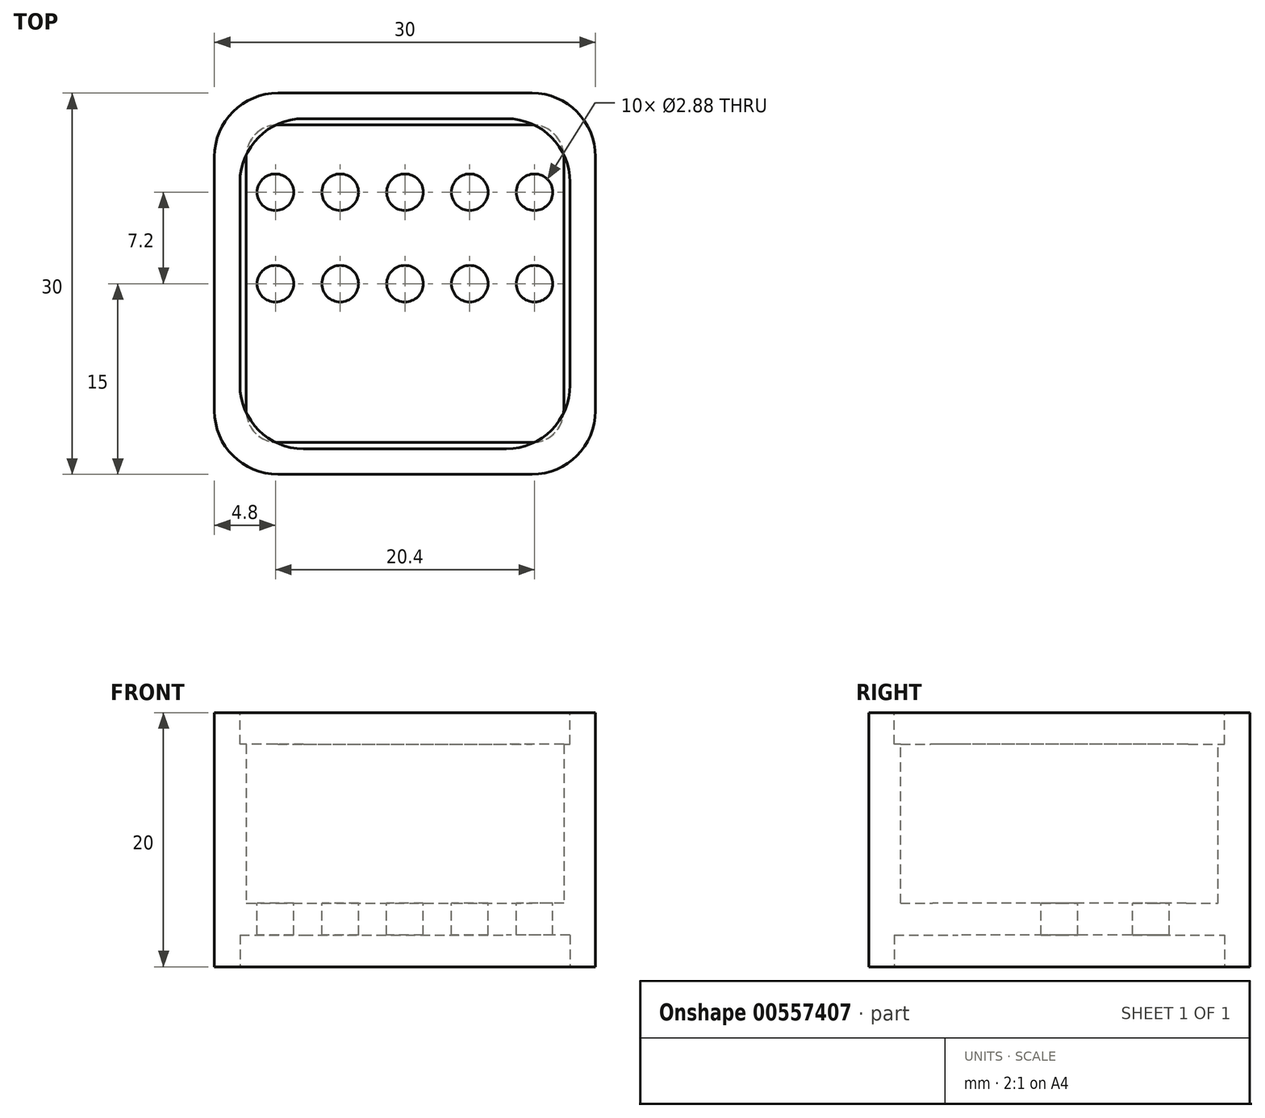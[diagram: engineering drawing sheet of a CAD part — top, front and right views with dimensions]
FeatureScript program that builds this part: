
annotation { "Feature Type Name" : "Feature", "Feature Type Description" : "" }
export const myFeature = defineFeature(function(context is Context, id is Id, definition is map)
    precondition{}
    {
        {
            var Q0;
            Q0=qCreatedBy(makeId("Top.planeOp"),FACE);
            var sketch = newSketch(context, id + "F0", { "sketchPlane" : qUnion([Q0])});
            skLineSegment(sketch, "E0.bottom", {"start": v(-15, 15) * mm, "end": v(15, 15) * mm});
            skLineSegment(sketch, "E0.top", {"start": v(-15, -15) * mm, "end": v(15, -15) * mm});
            skLineSegment(sketch, "E0.left", {"start": v(-15, 15) * mm, "end": v(-15, -15) * mm});
            skLineSegment(sketch, "E0.right", {"start": v(15, 15) * mm, "end": v(15, -15) * mm});
            skLineSegment(sketch, "E1.0", {"start": v(-13, 13) * mm, "end": v(13, 13) * mm, "construction": true});
            skLineSegment(sketch, "E1.1", {"start": v(-13, 13) * mm, "end": v(-13, -13) * mm, "construction": true});
            skLineSegment(sketch, "E1.2", {"start": v(-13, -13) * mm, "end": v(13, -13) * mm, "construction": true});
            skLineSegment(sketch, "E1.3", {"start": v(13, 13) * mm, "end": v(13, -13) * mm, "construction": true});
            skSolve(sketch);
        }
        {
            var Q0;
            Q0 = qSketchRegion(id + "F0", true);
            extrude(context, id + "F1", {"entities" : qUnion([Q0]), "depth" : 20 * mm, "offsetDistance" : 25 * mm});
        }
        {
            var Q0;
            Q0=makeQuery(id+"F0.imprint","IMPRINT",FACE,{"disambiguationData":[TD([[makeQuery(id+"F0.imprint","IMPRINT",EDGE,{"derivedFrom":sQuery(id+"F0.wireOp",EDGE,"E0.bottom")}),-1.0]])]});
            var sketch = newSketch(context, id + "F2", { "sketchPlane" : qUnion([Q0])});
            skLineSegment(sketch, "E2.0", {"start": v(-13, -13) * mm, "end": v(13, -13) * mm});
            skLineSegment(sketch, "E3.0", {"start": v(13, 13) * mm, "end": v(13, -13) * mm});
            skLineSegment(sketch, "E3.1", {"start": v(-13, 13) * mm, "end": v(13, 13) * mm});
            skLineSegment(sketch, "E3.2", {"start": v(-13, 13) * mm, "end": v(-13, -13) * mm});
            skSolve(sketch);
        }
        {
            var Q0;
            Q0 = qSketchRegion(id + "F2", true);
            extrude(context, id + "F3", {"entities" : qUnion([Q0]), "operationType" : NewBodyOperationType.REMOVE, "depth" : 2.5 * mm, "offsetDistance" : 25 * mm});
        }
        {
            var Q0;
            Q0=makeQuery(id+"F1.opExtrude","CAP_FACE",FACE,{"disambiguationData":[OSD([sQuery(id+"F0.wireOp",EDGE,"E0.bottom"),sQuery(id+"F0.wireOp",EDGE,"E0.top"),sQuery(id+"F0.wireOp",EDGE,"E0.left"),sQuery(id+"F0.wireOp",EDGE,"E0.right")])],"isStart":false});
            var sketch = newSketch(context, id + "F4", { "sketchPlane" : qUnion([Q0])});
            skLineSegment(sketch, "E4.0", {"start": v(-13, 13) * mm, "end": v(-13, -13) * mm});
            skLineSegment(sketch, "E4.1", {"start": v(-13, -13) * mm, "end": v(13, -13) * mm});
            skLineSegment(sketch, "E4.2", {"start": v(13, 13) * mm, "end": v(13, -13) * mm});
            skLineSegment(sketch, "E4.3", {"start": v(-13, 13) * mm, "end": v(13, 13) * mm});
            skSolve(sketch);
        }
        {
            var Q0;
            Q0 = qSketchRegion(id + "F4", true);
            extrude(context, id + "F5", {"entities" : qUnion([Q0]), "operationType" : NewBodyOperationType.REMOVE, "oppositeDirection" : true, "depth" : 2.5 * mm, "offsetDistance" : 25 * mm});
        }
        {
            var Q0;
            Q0=makeQuery(id+"F1.opExtrude","SWEPT_EDGE",EDGE,{"disambiguationData":[OSD([sQuery(id+"F0.wireOp",EDGE,"E0.top"),sQuery(id+"F0.wireOp",EDGE,"E0.left")])]});
            var Q1;
            Q1=makeQuery(id+"F5.boolean.opBoolean","COPY",EDGE,{"derivedFrom":makeQuery(id+"F5.opExtrude","SWEPT_EDGE",EDGE,{"disambiguationData":[OSD([sQuery(id+"F4.wireOp",EDGE,"E4.0"),sQuery(id+"F4.wireOp",EDGE,"E4.1")])]})});
            var Q2;
            Q2=makeQuery(id+"F5.boolean.opBoolean","COPY",EDGE,{"derivedFrom":makeQuery(id+"F5.opExtrude","SWEPT_EDGE",EDGE,{"disambiguationData":[OSD([sQuery(id+"F4.wireOp",EDGE,"E4.0"),sQuery(id+"F4.wireOp",EDGE,"E4.3")])]})});
            var Q3;
            Q3=makeQuery(id+"F5.boolean.opBoolean","COPY",EDGE,{"derivedFrom":makeQuery(id+"F5.opExtrude","SWEPT_EDGE",EDGE,{"disambiguationData":[OSD([sQuery(id+"F4.wireOp",EDGE,"E4.1"),sQuery(id+"F4.wireOp",EDGE,"E4.2")])]})});
            var Q4;
            Q4=makeQuery(id+"F1.opExtrude","SWEPT_EDGE",EDGE,{"disambiguationData":[OSD([sQuery(id+"F0.wireOp",EDGE,"E0.top"),sQuery(id+"F0.wireOp",EDGE,"E0.right")])]});
            var Q5;
            Q5=makeQuery(id+"F1.opExtrude","SWEPT_EDGE",EDGE,{"disambiguationData":[OSD([sQuery(id+"F0.wireOp",EDGE,"E0.bottom"),sQuery(id+"F0.wireOp",EDGE,"E0.right")])]});
            var Q6;
            Q6=makeQuery(id+"F1.opExtrude","SWEPT_EDGE",EDGE,{"disambiguationData":[OSD([sQuery(id+"F0.wireOp",EDGE,"E0.bottom"),sQuery(id+"F0.wireOp",EDGE,"E0.left")])]});
            var Q7;
            Q7=makeQuery(id+"F5.boolean.opBoolean","COPY",EDGE,{"derivedFrom":makeQuery(id+"F5.opExtrude","SWEPT_EDGE",EDGE,{"disambiguationData":[OSD([sQuery(id+"F4.wireOp",EDGE,"E4.2"),sQuery(id+"F4.wireOp",EDGE,"E4.3")])]})});
            var Q8;
            Q8=makeQuery(id+"F3.boolean.opBoolean","COPY",EDGE,{"derivedFrom":makeQuery(id+"F3.opExtrude","SWEPT_EDGE",EDGE,{"disambiguationData":[OSD([sQuery(id+"F2.wireOp",EDGE,"E3.1"),sQuery(id+"F2.wireOp",EDGE,"E3.2")])]})});
            var Q9;
            Q9=makeQuery(id+"F3.boolean.opBoolean","COPY",EDGE,{"derivedFrom":makeQuery(id+"F3.opExtrude","SWEPT_EDGE",EDGE,{"disambiguationData":[OSD([sQuery(id+"F2.wireOp",EDGE,"E2.0"),sQuery(id+"F2.wireOp",EDGE,"E3.0")])]})});
            var Q10;
            Q10=makeQuery(id+"F3.boolean.opBoolean","COPY",EDGE,{"derivedFrom":makeQuery(id+"F3.opExtrude","SWEPT_EDGE",EDGE,{"disambiguationData":[OSD([sQuery(id+"F2.wireOp",EDGE,"E2.0"),sQuery(id+"F2.wireOp",EDGE,"E3.2")])]})});
            var Q11;
            Q11=makeQuery(id+"F3.boolean.opBoolean","COPY",EDGE,{"derivedFrom":makeQuery(id+"F3.opExtrude","SWEPT_EDGE",EDGE,{"disambiguationData":[OSD([sQuery(id+"F2.wireOp",EDGE,"E3.0"),sQuery(id+"F2.wireOp",EDGE,"E3.1")])]})});
            fillet(context, id + "F6", {"entities" : qUnion([Q0, Q1, Q2, Q3, Q4, Q5, Q6, Q7, Q8, Q9, Q10, Q11]), "radius" : 5 * mm, "tangentPropagation" : true, "allowEdgeOverflow" : false});
        }
        {
            var Q0;
            Q0=makeQuery(id+"F5.boolean.opBoolean","COPY",FACE,{"derivedFrom":makeQuery(id+"F5.opExtrude","CAP_FACE",FACE,{"disambiguationData":[OSD([sQuery(id+"F4.wireOp",EDGE,"E4.0"),sQuery(id+"F4.wireOp",EDGE,"E4.1"),sQuery(id+"F4.wireOp",EDGE,"E4.2"),sQuery(id+"F4.wireOp",EDGE,"E4.3")])],"isStart":false})});
            shell(context, id + "F7", {"entities" : qUnion([Q0]), "thickness" : 2.5 * mm});
        }
        {
            var Q0;
            Q0=makeQuery(id+"F7.opShell","OFFSET_FACE",FACE,{"disambiguationData":[OSD([sQuery(id+"F2.wireOp",EDGE,"E2.0"),sQuery(id+"F2.wireOp",EDGE,"E3.0"),sQuery(id+"F2.wireOp",EDGE,"E3.1"),sQuery(id+"F2.wireOp",EDGE,"E3.2")])]});
            var sketch = newSketch(context, id + "F8", { "sketchPlane" : qUnion([Q0])});
            skCircle(sketch, "E5", {"center": v(0, 0) * mm, "radius": 1.44 * mm});
            skCircle(sketch, "E6.0.1.0", {"center": v(0, 7.2) * mm, "radius": 1.44 * mm});
            skCircle(sketch, "E6.1.0.0", {"center": v(5.1, 0) * mm, "radius": 1.44 * mm});
            skCircle(sketch, "E6.1.1.0", {"center": v(5.1, 7.2) * mm, "radius": 1.44 * mm});
            skCircle(sketch, "E6.2.0.0", {"center": v(10.2, 0) * mm, "radius": 1.44 * mm});
            skCircle(sketch, "E6.2.1.0", {"center": v(10.2, 7.2) * mm, "radius": 1.44 * mm});
            skLineSegment(sketch, "E6.direction1", {"start": v(0, 0) * mm, "end": v(5.1, 0) * mm, "construction": true});
            skLineSegment(sketch, "E6.direction2", {"start": v(0, 0) * mm, "end": v(0, 7.2) * mm, "construction": true});
            skCircle(sketch, "E7.MirrorC", {"center": v(-5.1, 0) * mm, "radius": 1.44 * mm});
            skCircle(sketch, "E8.MirrorC", {"center": v(-10.2, 0) * mm, "radius": 1.44 * mm});
            skCircle(sketch, "E9.MirrorC", {"center": v(-10.2, 7.2) * mm, "radius": 1.44 * mm});
            skCircle(sketch, "E10.MirrorC", {"center": v(-5.1, 7.2) * mm, "radius": 1.44 * mm});
            skSolve(sketch);
        }
        {
            var Q0;
            Q0 = qSketchRegion(id + "F8", true);
            extrude(context, id + "F9", {"entities" : qUnion([Q0]), "operationType" : NewBodyOperationType.REMOVE, "oppositeDirection" : true, "depth" : 25 * mm, "offsetDistance" : 25 * mm});
        }
    });
